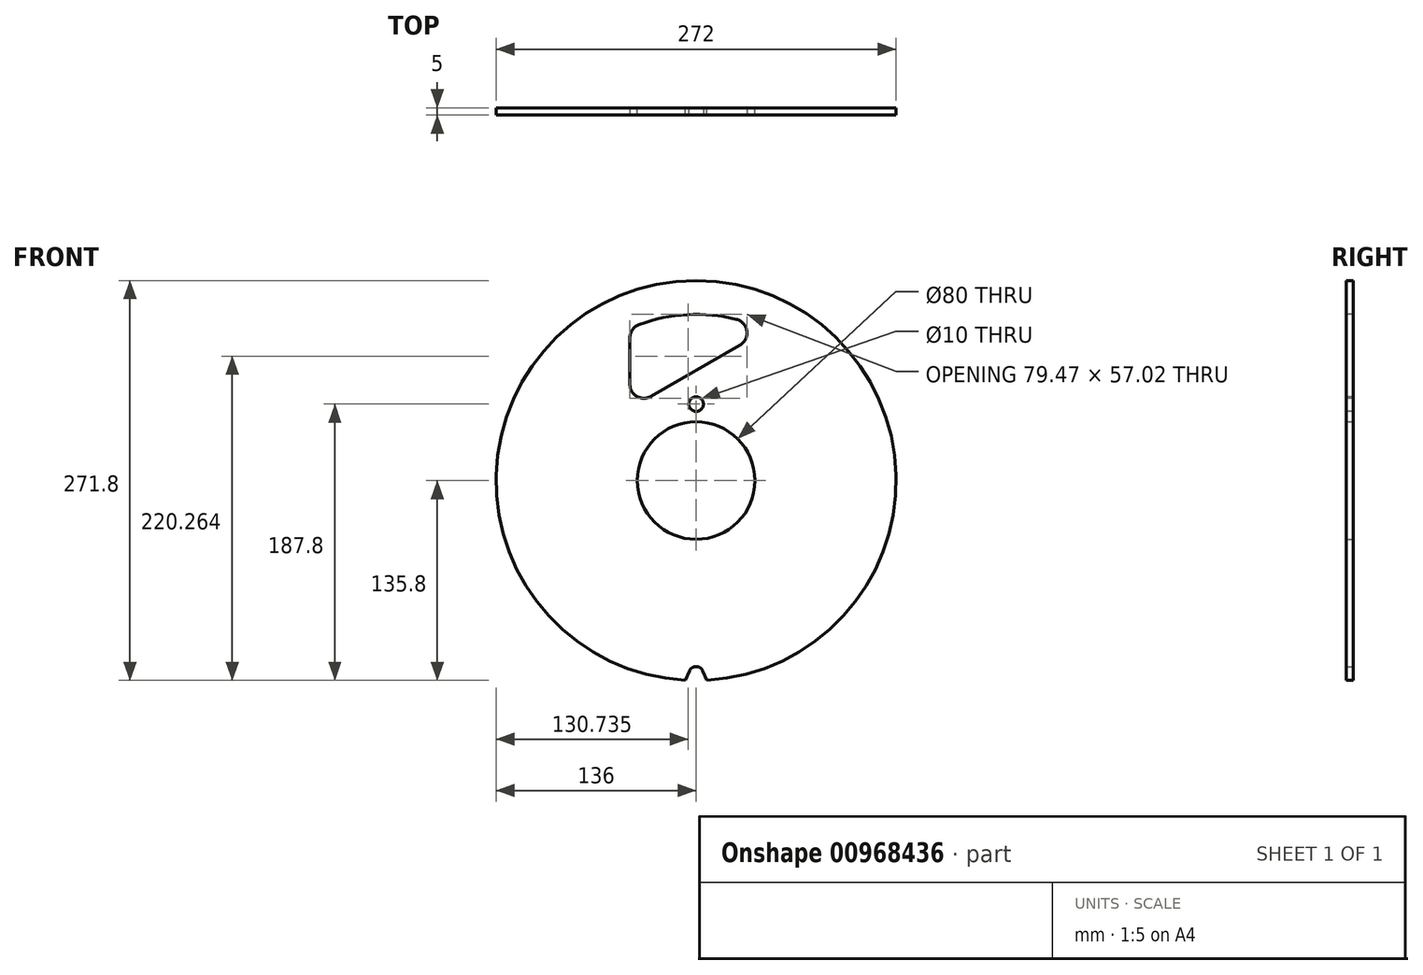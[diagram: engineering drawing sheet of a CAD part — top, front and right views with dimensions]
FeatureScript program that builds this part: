
annotation { "Feature Type Name" : "Feature", "Feature Type Description" : "" }
export const myFeature = defineFeature(function(context is Context, id is Id, definition is map)
    precondition{}
    {
        {
            var Q0;
            Q0=qCreatedBy(makeId("Front.planeOp"),FACE);
            var sketch = newSketch(context, id + "F0", { "sketchPlane" : qUnion([Q0])});
            skArc(sketch, "E0", {"start": v(7.36, -135.8) * mm, "mid": v(0, 136) * mm, "end": v(-7.36, -135.8) * mm});
            skCircle(sketch, "E1", {"center": v(0, 0) * mm, "radius": 131.5 * mm, "construction": true});
            skCircle(sketch, "E2", {"center": v(0, 0) * mm, "radius": 40 * mm});
            skCircle(sketch, "E3", {"center": v(0, 0) * mm, "radius": 52 * mm, "construction": true});
            skCircle(sketch, "E4", {"center": v(0, 52) * mm, "radius": 5 * mm});
            skLineSegment(sketch, "E5", {"start": v(0, -131.5) * mm, "end": v(0, -136) * mm, "construction": true});
            skLineSegment(sketch, "E6", {"start": v(-4.58, -129.49) * mm, "end": v(-7.44, -136) * mm});
            skLineSegment(sketch, "E7", {"start": v(4.58, -129.49) * mm, "end": v(7.44, -136) * mm});
            skLineSegment(sketch, "E8", {"start": v(-7.44, -136) * mm, "end": v(7.44, -136) * mm});
            skArc(sketch, "E9.trimOffspring", {"start": v(4.58, -129.49) * mm, "mid": v(0, -126.5) * mm, "end": v(-4.58, -129.49) * mm});
            skLineSegment(sketch, "E10", {"start": v(-45, 65.45) * mm, "end": v(-45, 97.22) * mm});
            skLineSegment(sketch, "E11", {"start": v(-30.75, 57.23) * mm, "end": v(29.81, 92.2) * mm});
            skArc(sketch, "E12", {"start": v(27.36, 109.64) * mm, "mid": v(-5.96, 112.84) * mm, "end": v(-38.76, 106.15) * mm});
            skPoint(sketch, "E13.visualSharp", {"position": v(-45, 103.65) * mm});
            skArc(sketch, "E13.filletArc", {"start": v(-38.76, 106.15) * mm, "mid": v(-43.28, 102.67) * mm, "end": v(-45, 97.22) * mm});
            skPoint(sketch, "E14.visualSharp", {"position": v(-45, 49) * mm});
            skArc(sketch, "E14.filletArc", {"start": v(-45, 65.45) * mm, "mid": v(-40.25, 57.23) * mm, "end": v(-30.75, 57.23) * mm});
            skPoint(sketch, "E15.visualSharp", {"position": v(47.62, 102.48) * mm});
            skArc(sketch, "E15.filletArc", {"start": v(29.81, 92.2) * mm, "mid": v(34.47, 101.74) * mm, "end": v(27.36, 109.64) * mm});
            skSolve(sketch);
        }
        {
            var Q0;
            Q0=makeQuery(id+"F0.imprint","IMPRINT",FACE,{"disambiguationData":[TD([[makeQuery(id+"F0.imprint","IMPRINT",EDGE,{"derivedFrom":sQuery(id+"F0.wireOp",EDGE,"E4")}),1.0]])]});
            var Q1;
            {var subQ1=sQuery(id+"F0.wireOp",EDGE,"E0");Q1=makeQuery(id+"F0.imprint","IMPRINT",FACE,{"disambiguationData":[TD([[makeQuery(id+"F0.imprint","IMPRINT",EDGE,{"derivedFrom":subQ1}),1.0]])]});}
            var Q2;
            Q2=makeQuery(id+"F0.imprint","IMPRINT",FACE,{"disambiguationData":[TD([[makeQuery(id+"F0.imprint","IMPRINT",EDGE,{"derivedFrom":sQuery(id+"F0.wireOp",EDGE,"E10")}),-1.0]])]});
            var Q3;
            {var subQ3=sQuery(id+"F0.wireOp",EDGE,"E8");Q3=makeQuery(id+"F0.imprint","IMPRINT",FACE,{"disambiguationData":[TD([[makeQuery(id+"F0.imprint","IMPRINT",EDGE,{"derivedFrom":subQ3}),1.0]])]});}
            extrude(context, id + "F1", {"entities" : qUnion([Q0, Q1, Q2, Q3]), "depth" : 5 * mm, "offsetDistance" : 25 * mm, "symmetric" : true});
        }
        {
            var Q0;
            Q0=makeQuery(id+"F0.imprint","IMPRINT",FACE,{"disambiguationData":[TD([[makeQuery(id+"F0.imprint","IMPRINT",EDGE,{"derivedFrom":sQuery(id+"F0.wireOp",EDGE,"E10")}),-1.0]])]});
            extrude(context, id + "F2", {"entities" : qUnion([Q0]), "operationType" : NewBodyOperationType.REMOVE, "oppositeDirection" : true, "depth" : 25 * mm, "offsetDistance" : 25 * mm, "symmetric" : true});
        }
        {
            var Q0;
            Q0=makeQuery(id+"F0.imprint","IMPRINT",FACE,{"disambiguationData":[TD([[makeQuery(id+"F0.imprint","IMPRINT",EDGE,{"derivedFrom":sQuery(id+"F0.wireOp",EDGE,"E4")}),1.0]])]});
            var Q1;
            Q1=sQuery(id+"F0.wireOp",EDGE,"E4");
            extrude(context, id + "F3", {"entities" : qUnion([Q0]), "operationType" : NewBodyOperationType.REMOVE, "surfaceEntities" : qUnion([Q1]), "oppositeDirection" : true, "depth" : 25 * mm, "offsetDistance" : 25 * mm, "symmetric" : true});
        }
        {
            var Q0;
            {var subQ3=sQuery(id+"F0.wireOp",EDGE,"E8");Q0=makeQuery(id+"F0.imprint","IMPRINT",FACE,{"disambiguationData":[TD([[makeQuery(id+"F0.imprint","IMPRINT",EDGE,{"derivedFrom":subQ3}),1.0]])]});}
            extrude(context, id + "F4", {"entities" : qUnion([Q0]), "operationType" : NewBodyOperationType.REMOVE, "depth" : 25 * mm, "offsetDistance" : 25 * mm, "symmetric" : true});
        }
    });
